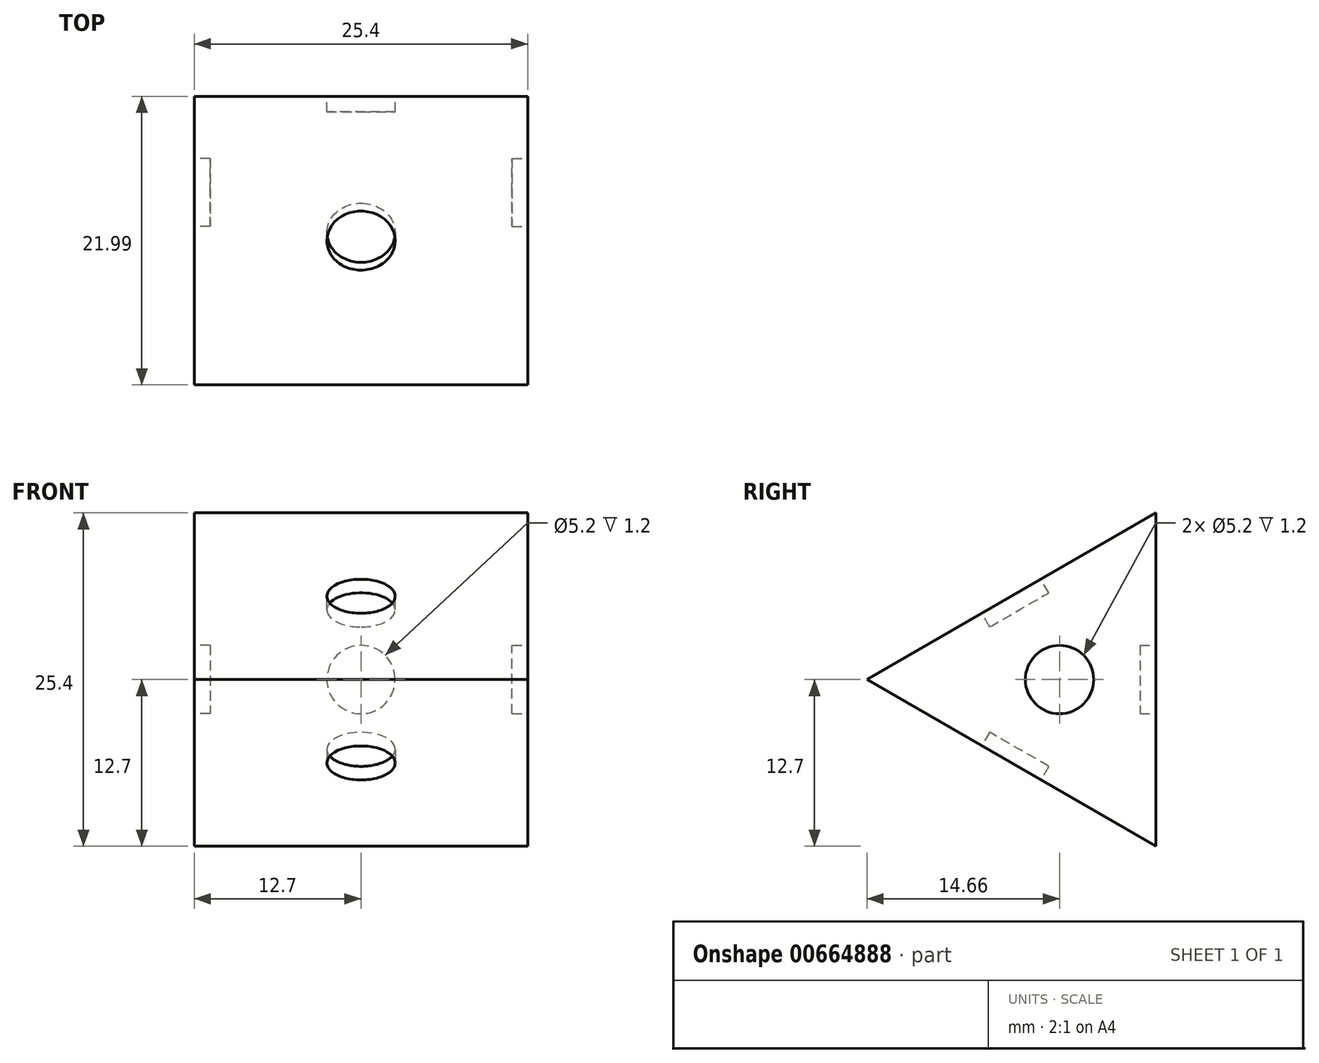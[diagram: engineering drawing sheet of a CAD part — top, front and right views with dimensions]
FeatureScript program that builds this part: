
annotation { "Feature Type Name" : "Feature", "Feature Type Description" : "" }
export const myFeature = defineFeature(function(context is Context, id is Id, definition is map)
    precondition{}
    {
        {
            var Q0;
            Q0=qCreatedBy(makeId("Right.planeOp"),FACE);
            var sketch = newSketch(context, id + "F0", { "sketchPlane" : qUnion([Q0])});
            skCircle(sketch, "E0.cCircle", {"center": v(0, 0) * mm, "radius": 7.33 * mm, "construction": true});
            skLineSegment(sketch, "E0.0", {"start": v(7.33, 12.7) * mm, "end": v(7.33, -12.7) * mm});
            skLineSegment(sketch, "E0.1", {"start": v(7.33, -12.7) * mm, "end": v(-14.66, 0) * mm});
            skLineSegment(sketch, "E0.2", {"start": v(-14.66, 0) * mm, "end": v(7.33, 12.7) * mm});
            skPoint(sketch, "E0.0.midPoint", {"position": v(7.33, 0) * mm});
            skSolve(sketch);
        }
        {
            var Q0;
            Q0=makeQuery(id+"F0.imprint","IMPRINT",FACE,{"disambiguationData":[TD([[makeQuery(id+"F0.imprint","IMPRINT",EDGE,{"derivedFrom":sQuery(id+"F0.wireOp",EDGE,"E0.0")}),-1.0]])]});
            extrude(context, id + "F1", {"entities" : qUnion([Q0]), "endBound" : BoundingType.SYMMETRIC, "depth" : 25.4 * mm, "offsetDistance" : 25 * mm});
        }
        {
            var Q0;
            Q0=makeQuery(id+"F1.opExtrude","SWEPT_FACE",FACE,{"disambiguationData":[OSD([sQuery(id+"F0.wireOp",EDGE,"E0.2")])]});
            var sketch = newSketch(context, id + "F2", { "sketchPlane" : qUnion([Q0])});
            skCircle(sketch, "E1", {"center": v(0, 0) * mm, "radius": 2.6 * mm});
            skSolve(sketch);
        }
        {
            var Q0;
            Q0=makeQuery(id+"F1.opExtrude","SWEPT_FACE",FACE,{"disambiguationData":[OSD([sQuery(id+"F0.wireOp",EDGE,"E0.0")])]});
            var sketch = newSketch(context, id + "F3", { "sketchPlane" : qUnion([Q0])});
            skCircle(sketch, "E2", {"center": v(0, 0) * mm, "radius": 2.6 * mm});
            skSolve(sketch);
        }
        {
            var Q0;
            Q0=makeQuery(id+"F1.opExtrude","SWEPT_FACE",FACE,{"disambiguationData":[OSD([sQuery(id+"F0.wireOp",EDGE,"E0.1")])]});
            var sketch = newSketch(context, id + "F4", { "sketchPlane" : qUnion([Q0])});
            skCircle(sketch, "E3", {"center": v(0, 0) * mm, "radius": 2.6 * mm});
            skSolve(sketch);
        }
        {
            var Q0;
            Q0=makeQuery(id+"F1.opExtrude","CAP_FACE",FACE,{"disambiguationData":[OSD([sQuery(id+"F0.wireOp",EDGE,"E0.0"),sQuery(id+"F0.wireOp",EDGE,"E0.1"),sQuery(id+"F0.wireOp",EDGE,"E0.2")])],"isStart":true});
            var sketch = newSketch(context, id + "F5", { "sketchPlane" : qUnion([Q0])});
            skCircle(sketch, "E4", {"center": v(0, 0) * mm, "radius": 2.6 * mm});
            skSolve(sketch);
        }
        {
            var Q0;
            Q0=makeQuery(id+"F1.opExtrude","CAP_FACE",FACE,{"disambiguationData":[OSD([sQuery(id+"F0.wireOp",EDGE,"E0.0"),sQuery(id+"F0.wireOp",EDGE,"E0.1"),sQuery(id+"F0.wireOp",EDGE,"E0.2")])],"isStart":false});
            var sketch = newSketch(context, id + "F6", { "sketchPlane" : qUnion([Q0])});
            skCircle(sketch, "E5", {"center": v(0, 0) * mm, "radius": 2.6 * mm});
            skSolve(sketch);
        }
        {
            var Q0;
            Q0=makeQuery(id+"F6.imprint","IMPRINT",FACE,{"disambiguationData":[TD([[makeQuery(id+"F6.imprint","IMPRINT",EDGE,{"derivedFrom":sQuery(id+"F6.wireOp",EDGE,"E5")}),1.0]])]});
            extrude(context, id + "F7", {"entities" : qUnion([Q0]), "operationType" : NewBodyOperationType.REMOVE, "oppositeDirection" : true, "depth" : 1.2 * mm, "offsetDistance" : 25 * mm});
        }
        {
            var Q0;
            Q0=makeQuery(id+"F4.imprint","IMPRINT",FACE,{"disambiguationData":[TD([[makeQuery(id+"F4.imprint","IMPRINT",EDGE,{"derivedFrom":sQuery(id+"F4.wireOp",EDGE,"E3")}),1.0]])]});
            extrude(context, id + "F8", {"entities" : qUnion([Q0]), "operationType" : NewBodyOperationType.REMOVE, "oppositeDirection" : true, "depth" : 1.2 * mm, "offsetDistance" : 25 * mm});
        }
        {
            var Q0;
            Q0=makeQuery(id+"F5.imprint","IMPRINT",FACE,{"disambiguationData":[TD([[makeQuery(id+"F5.imprint","IMPRINT",EDGE,{"derivedFrom":sQuery(id+"F5.wireOp",EDGE,"E4")}),1.0]])]});
            extrude(context, id + "F9", {"entities" : qUnion([Q0]), "operationType" : NewBodyOperationType.REMOVE, "oppositeDirection" : true, "depth" : 1.2 * mm, "offsetDistance" : 25 * mm});
        }
        {
            var Q0;
            Q0=makeQuery(id+"F3.imprint","IMPRINT",FACE,{"disambiguationData":[TD([[makeQuery(id+"F3.imprint","IMPRINT",EDGE,{"derivedFrom":sQuery(id+"F3.wireOp",EDGE,"E2")}),1.0]])]});
            extrude(context, id + "F10", {"entities" : qUnion([Q0]), "operationType" : NewBodyOperationType.REMOVE, "oppositeDirection" : true, "depth" : 1.2 * mm, "offsetDistance" : 25 * mm});
        }
        {
            var Q0;
            Q0=makeQuery(id+"F2.imprint","IMPRINT",FACE,{"disambiguationData":[TD([[makeQuery(id+"F2.imprint","IMPRINT",EDGE,{"derivedFrom":sQuery(id+"F2.wireOp",EDGE,"E1")}),1.0]])]});
            extrude(context, id + "F11", {"entities" : qUnion([Q0]), "operationType" : NewBodyOperationType.REMOVE, "oppositeDirection" : true, "depth" : 1.2 * mm, "offsetDistance" : 25 * mm});
        }
    });
